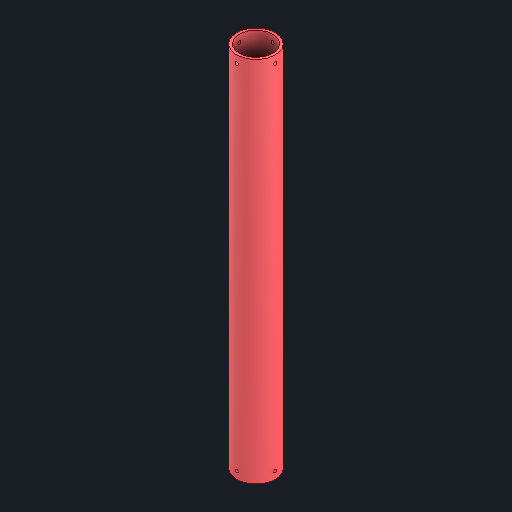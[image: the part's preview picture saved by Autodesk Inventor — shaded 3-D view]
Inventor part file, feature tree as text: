
AUTODESK INVENTOR PART (.ipt)
format: ipt  version: 2024 (Build 280153000, 153)  size: 115,200 bytes
history: native  units: in
note: dims shown in document units (in); Inventor stores cm internally (conversion verified against a paired STEP export)
features: mirror x1
ambient origin geometry x8: Origin, YZ Plane, XZ Plane, XY Plane, X Axis, Y Axis, Z Axis, Center Point
bodies: Solid1 (feature_tree)
feature tree (1):
  mirror  "Mirror1"
